# Revit family: Poussoirs Série 1621
name_source: partatom
category: Plumbing Fixtures
units: mm (PartAtom-declared; Revit-internal decimal feet)

## family parameters
Always vertical = Yes
Cut with Voids When Loaded = No
OmniClass Number = 23.45.00.00
OmniClass Title = Sanitary, Laundry, and Cleaning Equipment
Part Type = Normal
Room Calculation Point = No
Round Connector Dimension = Use Diameter
Shared = No
Work Plane-Based = Yes

## types (1)
- OLI_Pneumatique_Blanc
    BIM object developer = www.concepsysbim.com
    Default Elevation = 1219.2 mm  [stored 4 ft]
    Description = Poussoir pneumatique 3/6L blanc
    Manufacturer = REGIPLAST
    Model = Poussoirs  1621
    PLAQUE_Brève description = Poussoir pneumatique 3/6L blanc
    PLAQUE_Description technique = https://professionnels.regiplast.fr
    PLAQUE_Hauteur = 118 mm
    PLAQUE_Largeur = 127 mm
    PLAQUE_Longueur = 118 mm
    PLAQUE_Marque = REGIPLAST
    PLAQUE_Matériel = ABS
    PLAQUE_Modéle = Poussoirs  1621
    PLAQUE_Notice d'installation = https://professionnels.regiplast.fr
    PLAQUE_Référence du modèle = 1621
    PLAQUE_Site internet/Page web = https://www.regiplast.fr
    PLAQUE_Série = Blanc
    PLAQUE_Type d'actionnement = Pneumatique
    PLAQUE_Type de chasse = double-débit
    PLAQUE_Type/fonctionnement = Poussoir pneumatique double-débit
s
    PLAQUE_URL des données du produit = https://professionnels.regiplast.fr
    URL des données du produit = https://professionnels.regiplast.fr

note: [stored X ft] marks values corroborated as IEEE doubles in the binary element streams (Revit-internal decimal feet)

## geometry (parser evidence)
native form markers: Sweep x6
no freeform markers — native parametric forms only
